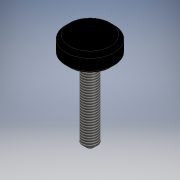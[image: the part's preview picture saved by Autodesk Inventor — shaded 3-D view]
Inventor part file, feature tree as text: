
AUTODESK INVENTOR PART (.ipt)
format: ipt  version: 2019 (Build 230136000, 136)  size: 127,488 bytes
history: native  units: mm
features: other x3, extrude x2, chamfer x2
ambient origin geometry x8: Origin, YZ Plane, XZ Plane, XY Plane, X Axis, Y Axis, Z Axis, Center Point
bodies: Solid1 (feature_tree), Body (feature_tree)
feature tree (7):
  extrude  "Base"  Depth=8.0mm
  extrude  "Head"  Depth=40.0mm TaperAngle=0.0deg
  chamfer  "Body Chamfer"  Distance=16.0mm
  chamfer  "Head Chamfer"  Distance=2.0mm
  other  "Body Cross Section"
  other  "Base Cross Section"
  other  "Head Cross Section"
